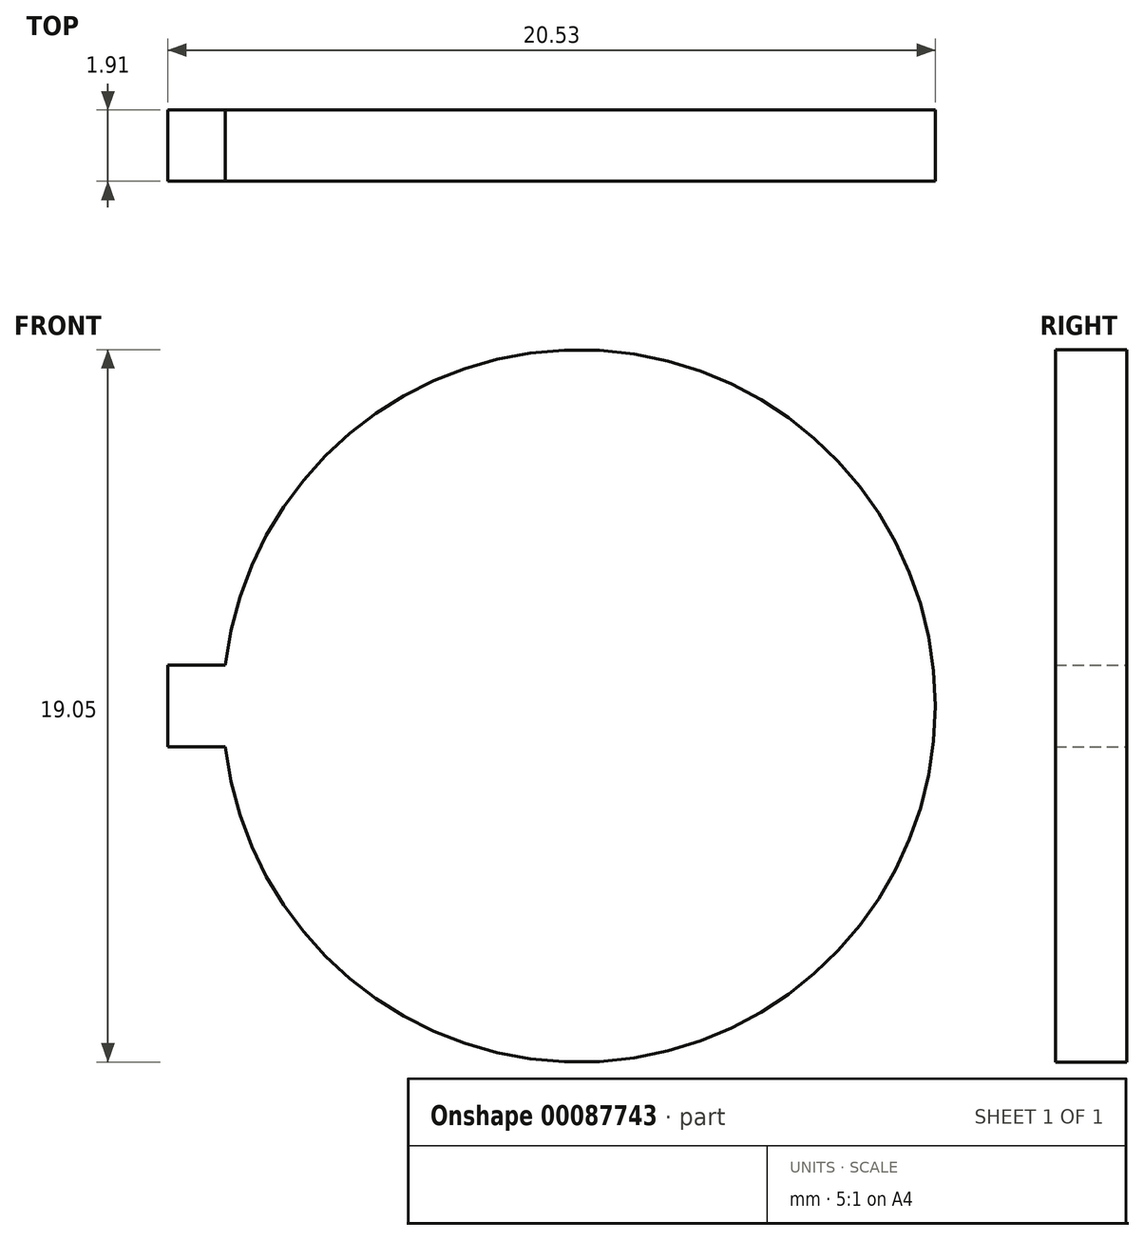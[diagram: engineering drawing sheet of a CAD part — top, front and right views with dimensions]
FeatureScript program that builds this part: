
annotation { "Feature Type Name" : "Feature", "Feature Type Description" : "" }
export const myFeature = defineFeature(function(context is Context, id is Id, definition is map)
    precondition{}
    {
        {
            var Q0;
            Q0=qCreatedBy(makeId("Front.planeOp"),FACE);
            var sketch = newSketch(context, id + "F0", { "sketchPlane" : qUnion([Q0])});
            skArc(sketch, "E0", {"start": v(-9.46, -1.1) * mm, "mid": v(9.53, 0) * mm, "end": v(-9.46, 1.1) * mm});
            skLineSegment(sketch, "E1", {"start": v(-11, 0) * mm, "end": v(-11, 1.1) * mm});
            skLineSegment(sketch, "E2", {"start": v(-11, 1.1) * mm, "end": v(-9.46, 1.1) * mm});
            skLineSegment(sketch, "E3", {"start": v(-11, 0) * mm, "end": v(-11, -1.1) * mm});
            skLineSegment(sketch, "E4", {"start": v(-11, -1.1) * mm, "end": v(-9.46, -1.1) * mm});
            skSolve(sketch);
        }
        {
            var Q0;
            Q0=makeQuery(id+"F0.imprint","IMPRINT",FACE,{"disambiguationData":[TD([[makeQuery(id+"F0.imprint","IMPRINT",EDGE,{"derivedFrom":sQuery(id+"F0.wireOp",EDGE,"E0")}),1.0]])]});
            extrude(context, id + "F1", {"entities" : qUnion([Q0]), "depth" : 1.9 * mm});
        }
    });
